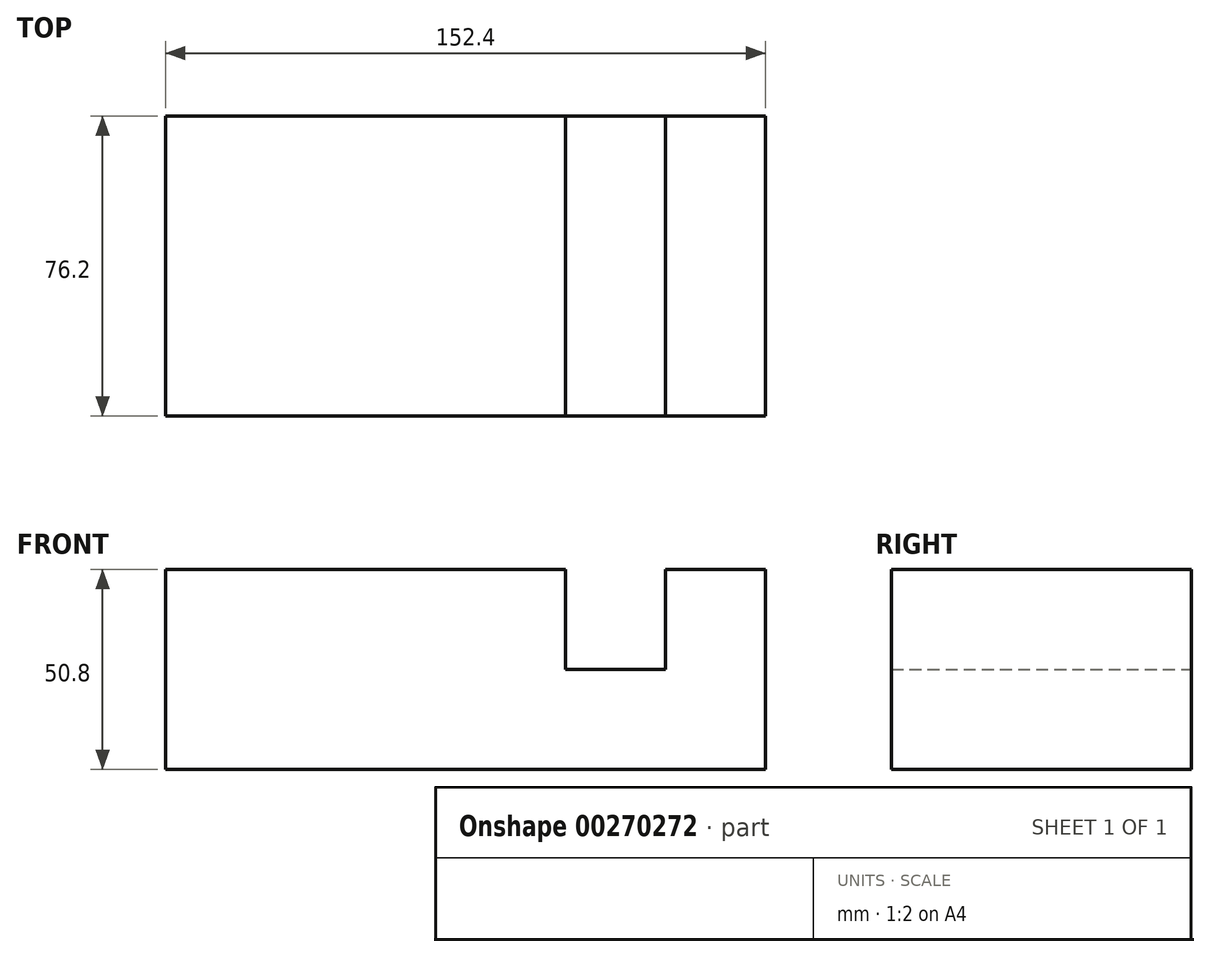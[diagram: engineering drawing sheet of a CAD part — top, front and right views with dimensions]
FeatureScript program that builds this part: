
annotation { "Feature Type Name" : "Feature", "Feature Type Description" : "" }
export const myFeature = defineFeature(function(context is Context, id is Id, definition is map)
    precondition{}
    {
        {
            var Q0;
            Q0=qCreatedBy(makeId("Front.planeOp"),FACE);
            var sketch = newSketch(context, id + "F0", { "sketchPlane" : qUnion([Q0])});
            skLineSegment(sketch, "E0.bottom", {"start": v(-101.6, -38.85) * mm, "end": v(0, -38.85) * mm});
            skLineSegment(sketch, "E0.top", {"start": v(-101.6, 11.95) * mm, "end": v(0, 11.95) * mm});
            skLineSegment(sketch, "E0.left", {"start": v(-101.6, -38.85) * mm, "end": v(-101.6, 11.95) * mm});
            skLineSegment(sketch, "E0.right", {"start": v(0, -38.85) * mm, "end": v(0, 11.95) * mm});
            skLineSegment(sketch, "E1.bottom", {"start": v(0, -38.85) * mm, "end": v(25.4, -38.85) * mm});
            skLineSegment(sketch, "E1.top", {"start": v(0, -13.45) * mm, "end": v(25.4, -13.45) * mm});
            skLineSegment(sketch, "E1.left", {"start": v(0, -38.85) * mm, "end": v(0, -13.45) * mm});
            skLineSegment(sketch, "E1.right", {"start": v(25.4, -38.85) * mm, "end": v(25.4, -13.45) * mm});
            skLineSegment(sketch, "E2.bottom", {"start": v(25.4, -38.85) * mm, "end": v(50.8, -38.85) * mm});
            skLineSegment(sketch, "E2.top", {"start": v(25.4, 11.95) * mm, "end": v(50.8, 11.95) * mm});
            skLineSegment(sketch, "E2.left", {"start": v(25.4, -38.85) * mm, "end": v(25.4, 11.95) * mm});
            skLineSegment(sketch, "E2.right", {"start": v(50.8, -38.85) * mm, "end": v(50.8, 11.95) * mm});
            skSolve(sketch);
        }
        {
            var Q0;
            Q0=makeQuery(id+"F0.imprint","IMPRINT",FACE,{"disambiguationData":[TD([[makeQuery(id+"F0.imprint","IMPRINT",EDGE,{"derivedFrom":sQuery(id+"F0.wireOp",EDGE,"E0.bottom")}),1.0]])]});
            var Q1;
            {var subQ0=sQuery(id+"F0.wireOp",EDGE,"E1.bottom");Q1=makeQuery(id+"F0.imprint","IMPRINT",FACE,{"disambiguationData":[TD([[makeQuery(id+"F0.imprint","IMPRINT",EDGE,{"derivedFrom":subQ0}),1.0]])]});}
            var Q2;
            {var subQ3=sQuery(id+"F0.wireOp",EDGE,"E2.bottom");Q2=makeQuery(id+"F0.imprint","IMPRINT",FACE,{"disambiguationData":[TD([[makeQuery(id+"F0.imprint","IMPRINT",EDGE,{"derivedFrom":subQ3}),1.0]])]});}
            extrude(context, id + "F1", {"entities" : qUnion([Q0, Q1, Q2]), "depth" : 76.2 * mm});
        }
    });
